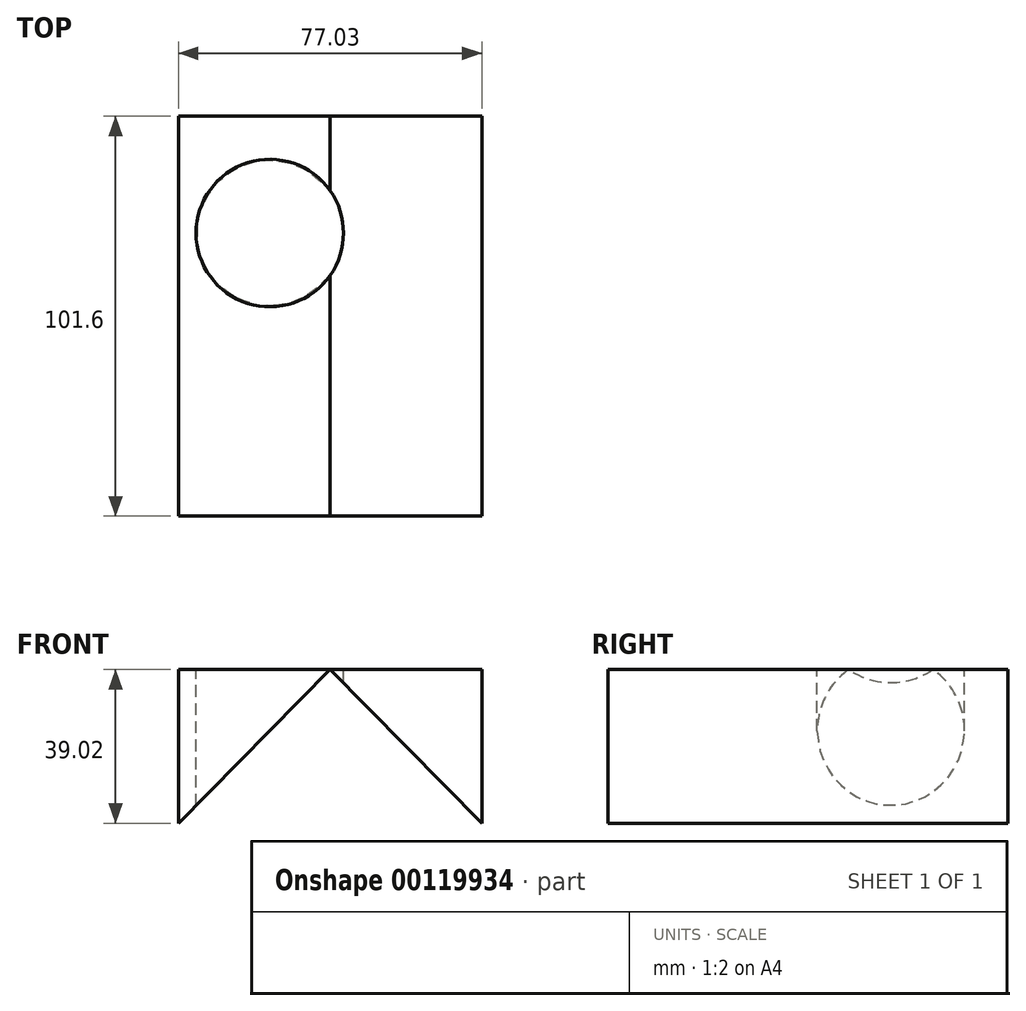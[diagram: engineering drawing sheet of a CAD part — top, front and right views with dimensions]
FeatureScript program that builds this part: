
annotation { "Feature Type Name" : "Feature", "Feature Type Description" : "" }
export const myFeature = defineFeature(function(context is Context, id is Id, definition is map)
    precondition{}
    {
        {
            var Q0;
            Q0=qCreatedBy(makeId("Front.planeOp"),FACE);
            var sketch = newSketch(context, id + "F0", { "sketchPlane" : qUnion([Q0])});
            skLineSegment(sketch, "E0.bottom", {"start": v(-64.95, 39.02) * mm, "end": v(12.08, 39.02) * mm});
            skLineSegment(sketch, "E0.top", {"start": v(-64.95, 0) * mm, "end": v(12.08, 0) * mm});
            skLineSegment(sketch, "E0.left", {"start": v(-64.95, 39.02) * mm, "end": v(-64.95, 0) * mm});
            skLineSegment(sketch, "E0.right", {"start": v(12.08, 39.02) * mm, "end": v(12.08, 0) * mm});
            skSolve(sketch);
        }
        {
            var Q0;
            Q0 = qSketchRegion(id + "F0", true);
            extrude(context, id + "F1", {"entities" : qUnion([Q0]), "depth" : 101.6 * mm});
        }
        {
            var Q0;
            Q0=makeQuery(id+"F1.opExtrude","SWEPT_FACE",FACE,{"disambiguationData":[OSD([sQuery(id+"F0.wireOp",EDGE,"E0.bottom")])]});
            var sketch = newSketch(context, id + "F2", { "sketchPlane" : qUnion([Q0])});
            skCircle(sketch, "E1", {"center": v(-41.78, -29.67) * mm, "radius": 18.73 * mm});
            skLineSegment(sketch, "E2.bottom", {"start": v(-23.05, -63.41) * mm, "end": v(-4.48, -63.41) * mm});
            skLineSegment(sketch, "E2.top", {"start": v(-23.05, -79.88) * mm, "end": v(-4.48, -79.88) * mm});
            skLineSegment(sketch, "E2.left", {"start": v(-23.05, -63.41) * mm, "end": v(-23.05, -79.88) * mm});
            skLineSegment(sketch, "E2.right", {"start": v(-4.48, -63.41) * mm, "end": v(-4.48, -79.88) * mm});
            skSolve(sketch);
        }
        {
            var Q0;
            Q0=makeQuery(id+"F2.imprint","IMPRINT",FACE,{"disambiguationData":[TD([[makeQuery(id+"F2.imprint","IMPRINT",EDGE,{"derivedFrom":sQuery(id+"F2.wireOp",EDGE,"E1")}),1.0]])]});
            extrude(context, id + "F3", {"entities" : qUnion([Q0]), "operationType" : NewBodyOperationType.REMOVE, "endBound" : BoundingType.THROUGH_ALL, "oppositeDirection" : true, "depth" : 25.4 * mm});
        }
        {
            var Q0;
            Q0=makeQuery(id+"F1.opExtrude","CAP_FACE",FACE,{"disambiguationData":[OSD([sQuery(id+"F0.wireOp",EDGE,"E0.bottom"),sQuery(id+"F0.wireOp",EDGE,"E0.top"),sQuery(id+"F0.wireOp",EDGE,"E0.left"),sQuery(id+"F0.wireOp",EDGE,"E0.right")])],"isStart":false});
            var sketch = newSketch(context, id + "F4", { "sketchPlane" : qUnion([Q0])});
            skLineSegment(sketch, "E3", {"start": v(-64.95, 0) * mm, "end": v(-26.43, 39.02) * mm});
            skLineSegment(sketch, "E4", {"start": v(-26.43, 39.02) * mm, "end": v(12.08, 0) * mm});
            skLineSegment(sketch, "E5", {"start": v(12.08, 0) * mm, "end": v(-64.95, 0) * mm});
            skSolve(sketch);
        }
        {
            var Q0;
            Q0=makeQuery(id+"F4.imprint","IMPRINT",FACE,{"disambiguationData":[TD([[makeQuery(id+"F4.imprint","IMPRINT",EDGE,{"derivedFrom":sQuery(id+"F4.wireOp",EDGE,"E3")}),-1.0]])]});
            extrude(context, id + "F5", {"entities" : qUnion([Q0]), "operationType" : NewBodyOperationType.REMOVE, "endBound" : BoundingType.THROUGH_ALL, "oppositeDirection" : true, "depth" : 25.4 * mm});
        }
    });
